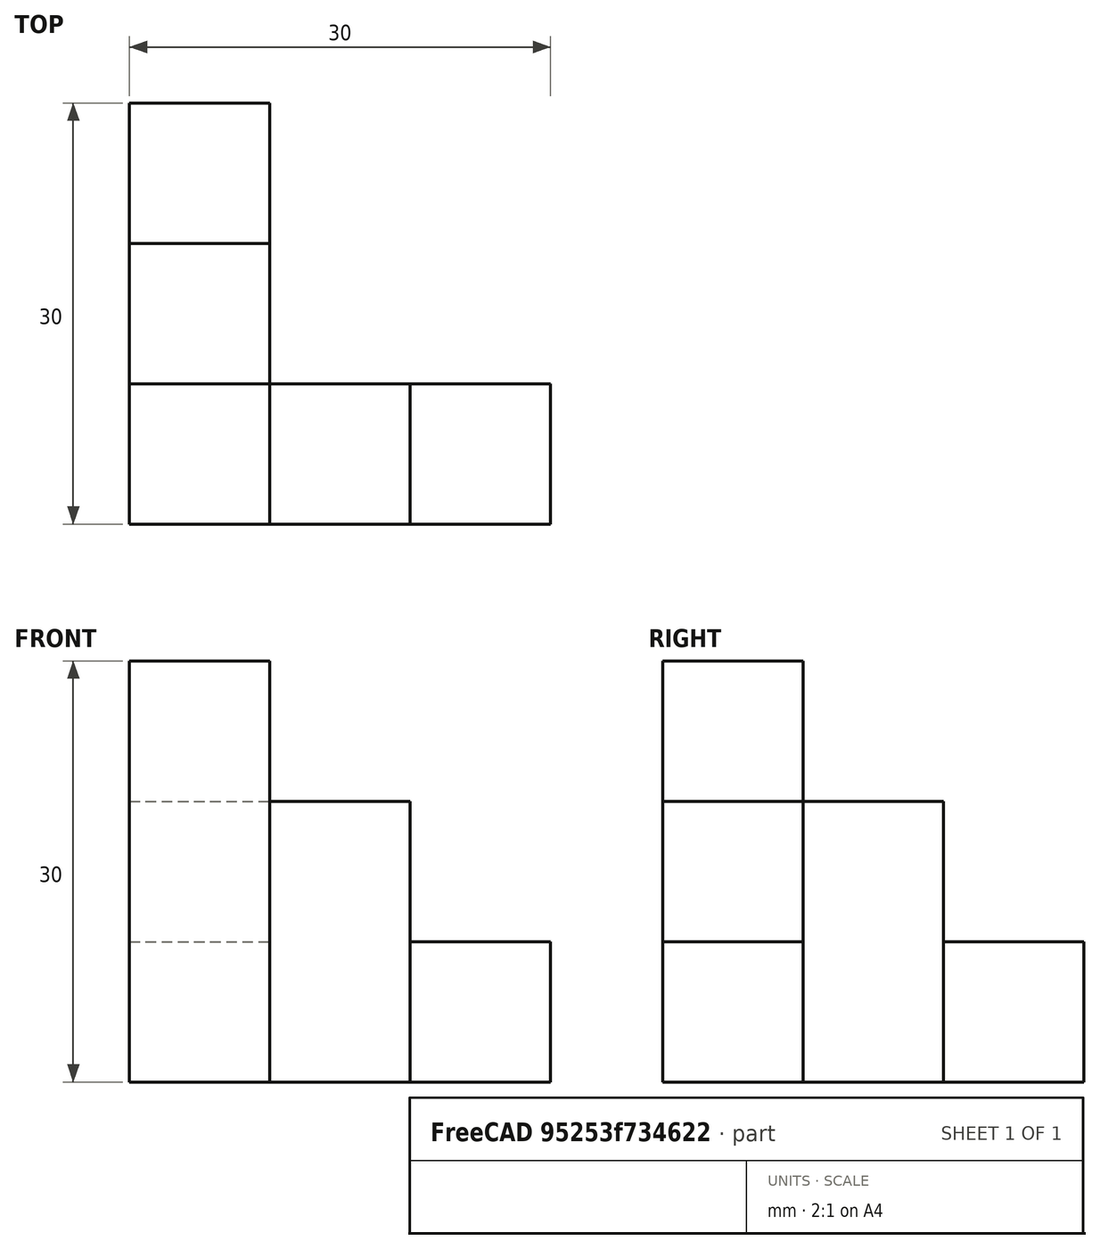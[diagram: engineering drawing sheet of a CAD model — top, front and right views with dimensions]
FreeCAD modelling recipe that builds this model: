
FCSTD DOCUMENT  (FreeCAD 0.21R33771 (Git))
Label: OJT1_T04R01_qbert3nivells
License: All rights reserved
LicenseURL: http://en.wikipedia.org/wiki/All_rights_reserved
objects: Part::Box×5
note: 5 computed .brp shape members not serialized (recipe doc carries the construction recipe); baked Part::Feature solids carry a one-line shape summary decoded from their .brp

FEATURE [Part::Box] Box  label="nivell1_cub1"
  AttacherType = Attacher::AttachEngine3D
  Height = 30
  Length = 10
  Width = 10
FEATURE [Part::Box] Box001  label="nivell2_cub1"
  AttacherType = Attacher::AttachEngine3D
  Height = 20
  Length = 10
  Placement = pos=(10,0,0) rot=(0,0,1;0rad)
  Width = 10
FEATURE [Part::Box] Box002  label="nivell2_cub2"
  AttacherType = Attacher::AttachEngine3D
  Height = 20
  Length = 10
  Placement = pos=(0,10,0) rot=(0,0,1;0rad)
  Width = 10
FEATURE [Part::Box] Box003  label="nivell3_cub1"
  AttacherType = Attacher::AttachEngine3D
  Height = 10
  Length = 10
  Placement = pos=(20,0,0) rot=(0,0,1;0rad)
  Width = 10
FEATURE [Part::Box] Box004  label="nivell3_cub2"
  AttacherType = Attacher::AttachEngine3D
  Height = 10
  Length = 10
  Placement = pos=(0,20,0) rot=(0,0,1;0rad)
  Width = 10
